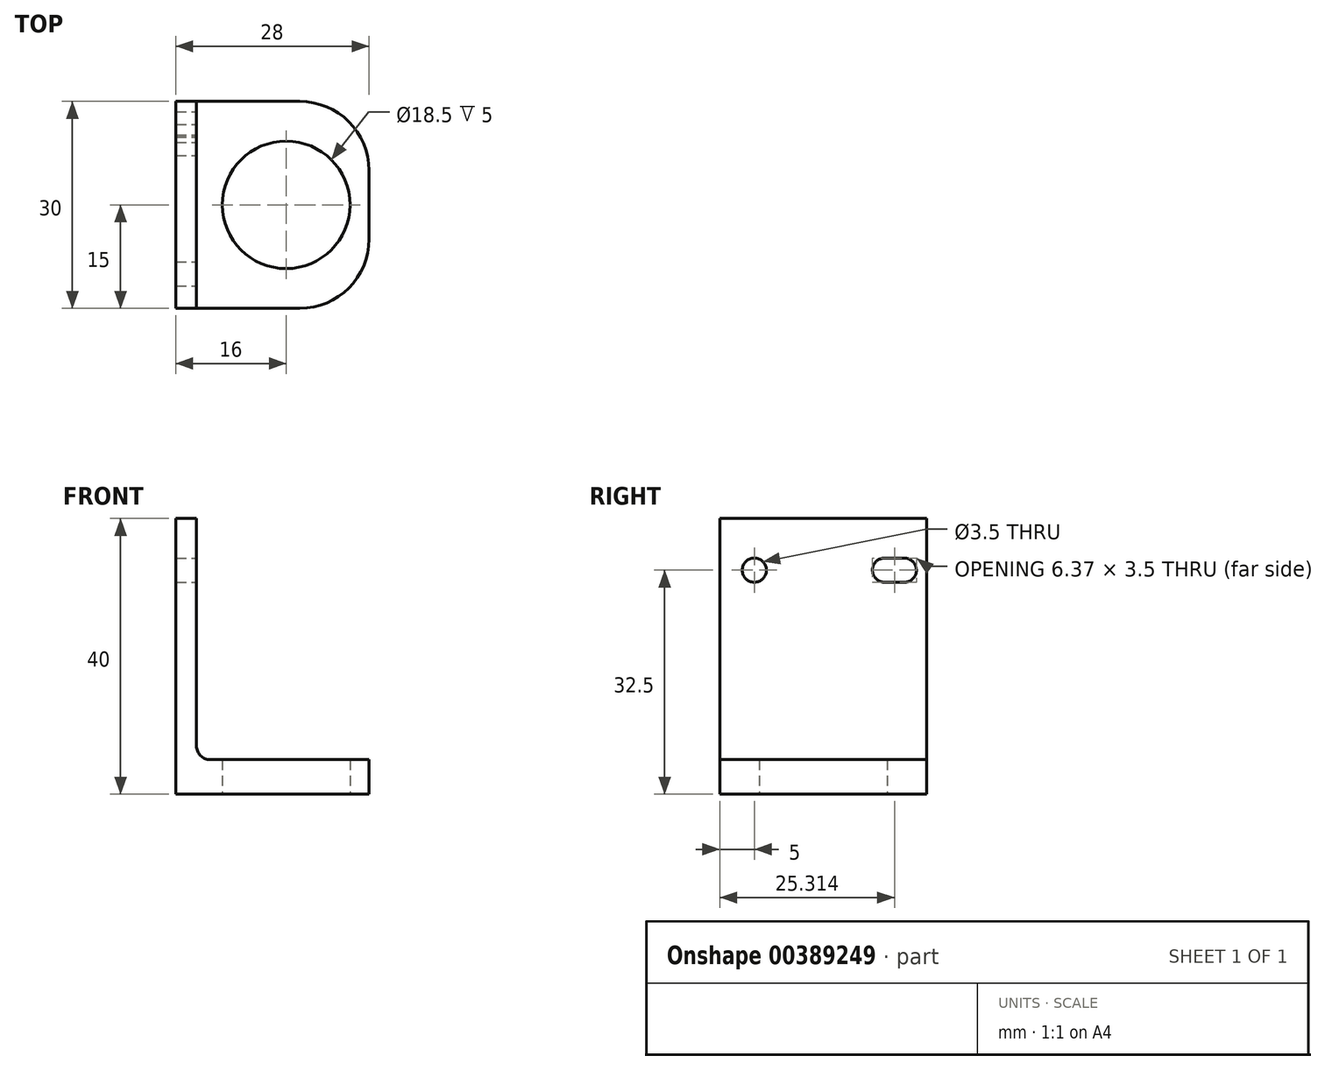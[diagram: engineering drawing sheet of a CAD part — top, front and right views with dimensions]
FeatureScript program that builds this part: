
annotation { "Feature Type Name" : "Feature", "Feature Type Description" : "" }
export const myFeature = defineFeature(function(context is Context, id is Id, definition is map)
    precondition{}
    {
        {
            var Q0;
            Q0=qCreatedBy(makeId("Top.planeOp"),FACE);
            var sketch = newSketch(context, id + "F0", { "sketchPlane" : qUnion([Q0])});
            skLineSegment(sketch, "E0.bottom", {"start": v(0, 0) * mm, "end": v(-28, 0) * mm});
            skLineSegment(sketch, "E0.top", {"start": v(0, 30) * mm, "end": v(-28, 30) * mm});
            skLineSegment(sketch, "E0.left", {"start": v(0, 0) * mm, "end": v(0, 30) * mm});
            skLineSegment(sketch, "E0.right", {"start": v(-28, 0) * mm, "end": v(-28, 30) * mm});
            skLineSegment(sketch, "E1", {"start": v(-25, 30) * mm, "end": v(-25, 0) * mm});
            skCircle(sketch, "E2", {"center": v(-12, 15) * mm, "radius": 9.25 * mm});
            skSolve(sketch);
        }
        {
            var Q0;
            Q0 = qSketchRegion(id + "F0", true);
            extrude(context, id + "F1", {"entities" : qUnion([Q0]), "depth" : 5 * mm});
        }
        {
            var Q0;
            {var subQ0=sQuery(id+"F0.wireOp",EDGE,"E0.right");Q0=makeQuery(id+"F0.imprint","IMPRINT",FACE,{"disambiguationData":[TD([[makeQuery(id+"F0.imprint","IMPRINT",EDGE,{"derivedFrom":subQ0}),-1.0]])]});}
            extrude(context, id + "F2", {"entities" : qUnion([Q0]), "operationType" : NewBodyOperationType.ADD, "depth" : 40 * mm});
        }
        {
            var Q0;
            Q0=makeQuery(id+"F1.opExtrude","SWEPT_EDGE",EDGE,{"disambiguationData":[OSD([sQuery(id+"F0.wireOp",EDGE,"E0.bottom"),sQuery(id+"F0.wireOp",EDGE,"E0.left")])]});
            var Q1;
            Q1=makeQuery(id+"F1.opExtrude","SWEPT_EDGE",EDGE,{"disambiguationData":[OSD([sQuery(id+"F0.wireOp",EDGE,"E0.top"),sQuery(id+"F0.wireOp",EDGE,"E0.left")])]});
            fillet(context, id + "F3", {"entities" : qUnion([Q0, Q1]), "radius" : 10 * mm, "tangentPropagation" : true, "allowEdgeOverflow" : false});
        }
        {
            var Q0;
            Q0=makeQuery(id+"F2.opExtrude","SWEPT_FACE",FACE,{"disambiguationData":[OSD([sQuery(id+"F0.wireOp",EDGE,"E1")])]});
            var sketch = newSketch(context, id + "F4", { "sketchPlane" : qUnion([Q0])});
            skLineSegment(sketch, "E3", {"start": v(0, 32.5) * mm, "end": v(30, 32.5) * mm, "construction": true});
            skCircle(sketch, "E4", {"center": v(5, 32.5) * mm, "radius": 1.75 * mm});
            skCircle(sketch, "E5", {"center": v(25, 32.5) * mm, "radius": 1.75 * mm});
            skCircle(sketch, "E6", {"center": v(23.88, 32.5) * mm, "radius": 1.75 * mm});
            skCircle(sketch, "E7", {"center": v(26.75, 32.5) * mm, "radius": 1.75 * mm});
            skLineSegment(sketch, "E8", {"start": v(23.69, 34.24) * mm, "end": v(26.75, 34.25) * mm});
            skLineSegment(sketch, "E9", {"start": v(26.83, 30.75) * mm, "end": v(23.88, 30.75) * mm});
            skSolve(sketch);
        }
        {
            var Q0;
            Q0 = qSketchRegion(id + "F4", true);
            var Q1;
            {var subQ0=sQuery(id+"F4.wireOp",EDGE,"E7");var subQ1=sQuery(id+"F4.wireOp",EDGE,"E5");var subQ2=makeQuery(id+"F4.imprint","INTERSECT",VERTEX,{"disambiguationData":[OD(0.0)],"derivedFrom":[subQ1,subQ0]});Q1=makeQuery(id+"F4.imprint","IMPRINT",FACE,{"disambiguationData":[TD([[makeQuery(id+"F4.imprint","IMPRINT",EDGE,{"disambiguationData":[TD([[subQ2,1.0]])],"derivedFrom":subQ1}),1.0]])]});}
            var Q2;
            {var subQ0=sQuery(id+"F4.wireOp",EDGE,"E6");var subQ1=sQuery(id+"F4.wireOp",EDGE,"E5");var subQ2=makeQuery(id+"F4.imprint","INTERSECT",VERTEX,{"disambiguationData":[OD(0.0)],"derivedFrom":[subQ1,subQ0]});Q2=makeQuery(id+"F4.imprint","IMPRINT",FACE,{"disambiguationData":[TD([[makeQuery(id+"F4.imprint","IMPRINT",EDGE,{"disambiguationData":[TD([[subQ2,-1.0]])],"derivedFrom":subQ1}),1.0]])]});}
            var Q3;
            {var subQ0=sQuery(id+"F4.wireOp",EDGE,"E7");var subQ1=sQuery(id+"F4.wireOp",EDGE,"E6");var subQ2=makeQuery(id+"F4.imprint","INTERSECT",VERTEX,{"disambiguationData":[OD(0.0)],"derivedFrom":[subQ1,subQ0]});Q3=makeQuery(id+"F4.imprint","IMPRINT",FACE,{"disambiguationData":[TD([[makeQuery(id+"F4.imprint","IMPRINT",EDGE,{"disambiguationData":[TD([[subQ2,1.0]])],"derivedFrom":subQ1}),1.0]])]});}
            extrude(context, id + "F5", {"entities" : qUnion([Q0, Q1, Q2, Q3]), "operationType" : NewBodyOperationType.REMOVE, "endBound" : BoundingType.THROUGH_ALL, "oppositeDirection" : true, "depth" : 25 * mm});
        }
        {
            var Q0;
            Q0=makeQuery(id+"F2.boolean.opBoolean","INTERSECT",EDGE,{"derivedFrom":[makeQuery(id+"F1.opExtrude","CAP_FACE",FACE,{"disambiguationData":[OSD([sQuery(id+"F0.wireOp",EDGE,"E0.bottom"),sQuery(id+"F0.wireOp",EDGE,"E0.top"),sQuery(id+"F0.wireOp",EDGE,"E0.left"),sQuery(id+"F0.wireOp",EDGE,"E0.right"),sQuery(id+"F0.wireOp",EDGE,"E2")])],"isStart":false}),makeQuery(id+"F2.opExtrude","SWEPT_FACE",FACE,{"disambiguationData":[OSD([sQuery(id+"F0.wireOp",EDGE,"E1")])]})]});
            fillet(context, id + "F6", {"entities" : qUnion([Q0]), "radius" : 2 * mm, "tangentPropagation" : true, "allowEdgeOverflow" : false});
        }
    });
